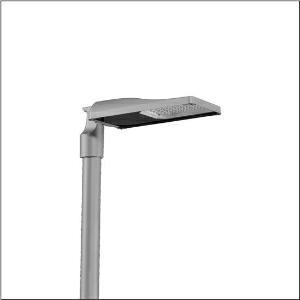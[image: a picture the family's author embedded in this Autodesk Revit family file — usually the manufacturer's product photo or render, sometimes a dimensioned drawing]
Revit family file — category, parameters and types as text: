
# Revit family: streetlight_sl_31_mini___st1_0a_5xh6d31a08ja_4a04
name_source: partatom
category: Lighting Fixtures
units: mm (PartAtom-declared; Revit-internal decimal feet)

## family parameters
Cut with Voids When Loaded = No
Host = Face
Light Source = No
Part Type = Normal
Room Calculation Point = No
Round Connector Dimension = Use Diameter
Shared = No

## types (1)
- --- (1 x LED, 12140 lm, 81.1 W, 3000K)
    Apparent Load = 81 VA
    CIE Flux Codes = 40 73 97 100 100
    Color Rendering = 70
    Color Temperature = 3000K
    Default Elevation = 1800 mm
    Description = Streetlight SL 31 mini, mast luminaire, primary light control with lens, of PMMA, primary optical cover: cover, of toughened safety glass, transparent, light distribution: ST1.0a, light emission: direct distribution, primary light characteristic: asymmetric, installation type: post-top, side-entry, LED, High Power LED, rated luminous flux: 12.140lm, luminous efficacy: 150lm/W, light colour: 730, colour temperature: 3000K, control: presetting dimming linear, flexible luminous flux parameterisation, time-dependent luminous flux control, constant luminous flux control, intelligent temperature release in ECG and LED module, overheat protection, with cable H07RN-F 2x 1.5mm², mains connection: 220..240V, AC, 50/60Hz, connection cable pre-assembled, cable length: 10,5m, start of lifetime: 81W, end of service life: 88W, reduction: 36W, luminaire housing, of diecast aluminium, powder-coated, Siteco® metallic grey (DB 702S), corrosivity category C5 high according to DIN EN ISO 12944, no sealing on luminaire upper side, inclination: -15°..+20° (post-top) | -20°..+20° (side-entry), adjustable in 5° steps, mast flange (76/60mm) included as standard, multi-level sealing system, sealing non-destructively replaceable, protection rating (complete): IP66, insulation class (complete): insulation class II (safety insulation), certification: CE, ENEC, ENEC+, VDE, UKCA, impact resistance: IK09, permissible operating ambient temperature for outdoor applications: -40..+50°C, standard-compliant lighting for roads and squares, packaging unit: 1 piece

Light Distribution: ST1.0a
    Height = 76 mm
    Lamp = 1 x LED
    Lamp Light Flux = 12140 lm
    Lamp Power = 81.1 W
    Lamp count = 1
    Length = 547 mm
    Luminous efficacy = 150 lm/W
    Manufacturer = Siteco
    ModVariant = No
    Model = 5XH6D31A08JA
    Number of Poles = 1
    OnlyDefault = Yes
    Power Factor = 1
    Product Name = Streetlight SL 31 mini | ST1.0a
    Product group = mast luminaire | pylon top
    ProductGroupID = 6100
    Protection Class = Protection class II
    Protection Degree = IP 66
    RLX_Detail_Level = 1
    RLX_Emergency_Light_Flux = 0 lm
    RLX_Emergency_Type = 0
    RLX_Emergency_Type_DB = No
    RlxData = <blob elided: 40069 chars, md5=60fe457b>
    Socket = socket
    Standby Power = 0 W
    System Light Flux = 12140 lm
    System Power = 81 W
    Type Comments = factory setting: luminous flux: 100 % | dim-lin: 254 | 860 mA
    Type Image = l_1300326.jpg
    URL = http://relux.com
    VarID = @adj_008135
    Voltage = 0 V
    Weight = 0.00 kg
    Width = 265 mm

## geometry (parser evidence)
native form markers: Blend x4, Sweep x11
no freeform markers — native parametric forms only
